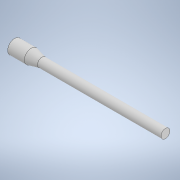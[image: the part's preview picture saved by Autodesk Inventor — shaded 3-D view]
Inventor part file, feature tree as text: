
AUTODESK INVENTOR PART (.ipt)
format: ipt  version: 2021 (Build 250183000, 183)  size: 102,400 bytes
history: native  units: mm
features: revolve x1, sketch x1
ambient origin geometry x8: Origin, YZ Plane, XZ Plane, XY Plane, X Axis, Y Axis, Z Axis, Center Point
bodies: Body1 (feature_tree)
feature tree (2):
  revolve  "Revolution1"  [1 undecoded]
  sketch  "Sketch2"  dims[d3=270.0mm d4=12.5mm d5=8.0mm d6=30.0mm d7=19.0mm d8=90.0deg]
note: 1 required parameter value undecoded (feature->parameter linkage not recoverable at this tier; creation-order binding heuristic only, values carry confidence <= 0.55)
